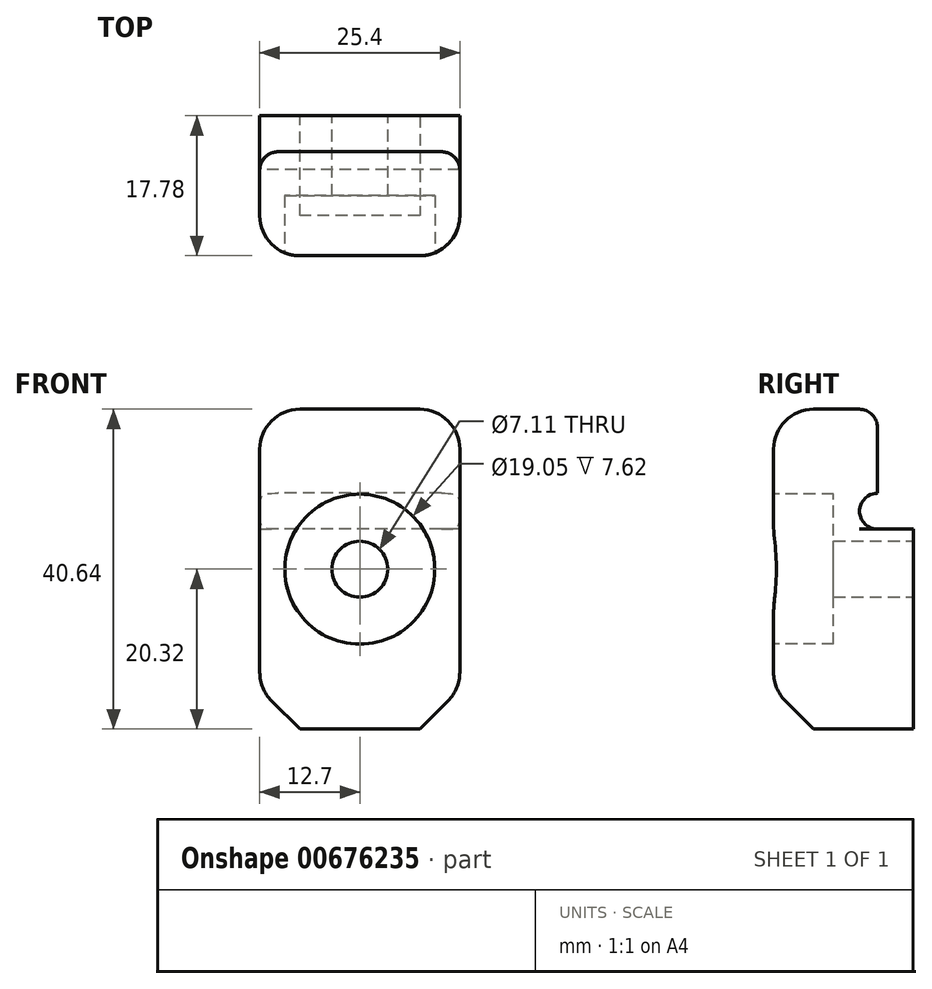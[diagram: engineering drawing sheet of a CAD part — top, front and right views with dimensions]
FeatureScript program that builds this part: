
annotation { "Feature Type Name" : "Feature", "Feature Type Description" : "" }
export const myFeature = defineFeature(function(context is Context, id is Id, definition is map)
    precondition{}
    {
        {
            var Q0;
            Q0=qCreatedBy(makeId("Right.planeOp"),FACE);
            var sketch = newSketch(context, id + "F0", { "sketchPlane" : qUnion([Q0])});
            skLineSegment(sketch, "E0.bottom", {"start": v(0, 0) * mm, "end": v(-4.57, 0) * mm});
            skLineSegment(sketch, "E0.top", {"start": v(0, -25.4) * mm, "end": v(-17.78, -25.4) * mm});
            skLineSegment(sketch, "E0.left", {"start": v(0, 0) * mm, "end": v(0, -25.4) * mm});
            skLineSegment(sketch, "E0.right", {"start": v(-17.78, 0) * mm, "end": v(-17.78, -25.4) * mm});
            skLineSegment(sketch, "E1.top", {"start": v(-17.78, 15.24) * mm, "end": v(-4.57, 15.24) * mm});
            skLineSegment(sketch, "E1.left", {"start": v(-17.78, 0) * mm, "end": v(-17.78, 15.24) * mm});
            skLineSegment(sketch, "E2", {"start": v(-9.82, 2.29) * mm, "end": v(19.83, 2.29) * mm, "construction": true});
            skArc(sketch, "E3", {"start": v(-4.57, 4.57) * mm, "mid": v(-6.86, 2.29) * mm, "end": v(-4.57, 0) * mm});
            skLineSegment(sketch, "E4.trimOffspring", {"start": v(-4.57, 4.57) * mm, "end": v(-4.57, 15.24) * mm});
            skSolve(sketch);
        }
        {
            var Q0;
            Q0=makeQuery(id+"F0.imprint","IMPRINT",FACE,{"disambiguationData":[TD([[makeQuery(id+"F0.imprint","IMPRINT",EDGE,{"derivedFrom":sQuery(id+"F0.wireOp",EDGE,"E0.bottom")}),1.0]])]});
            extrude(context, id + "F1", {"entities" : qUnion([Q0]), "depth" : 25.4 * mm, "offsetDistance" : 25.4 * mm});
        }
        {
            var Q0;
            Q0=makeQuery(id+"F1.opExtrude","SWEPT_FACE",FACE,{"disambiguationData":[OSD([sQuery(id+"F0.wireOp",EDGE,"E0.left")])]});
            var sketch = newSketch(context, id + "F2", { "sketchPlane" : qUnion([Q0])});
            skLineSegment(sketch, "E5", {"start": v(-12.7, 0) * mm, "end": v(-12.7, -25.4) * mm, "construction": true});
            skCircle(sketch, "E6", {"center": v(-12.7, -5.08) * mm, "radius": 3.56 * mm});
            skSolve(sketch);
        }
        {
            var Q0;
            Q0 = qSketchRegion(id + "F2", true);
            extrude(context, id + "F3", {"entities" : qUnion([Q0]), "operationType" : NewBodyOperationType.REMOVE, "endBound" : BoundingType.UP_TO_NEXT, "oppositeDirection" : true, "depth" : 25.4 * mm, "offsetDistance" : 25.4 * mm});
        }
        {
            var Q0;
            Q0=makeQuery(id+"F1.opExtrude","SWEPT_FACE",FACE,{"disambiguationData":[OSD([sQuery(id+"F0.wireOp",EDGE,"E0.right"),sQuery(id+"F0.wireOp",EDGE,"E1.left")])]});
            var sketch = newSketch(context, id + "F4", { "sketchPlane" : qUnion([Q0])});
            skCircle(sketch, "E7", {"center": v(12.7, -5.08) * mm, "radius": 9.52 * mm});
            skSolve(sketch);
        }
        {
            var Q0;
            Q0=makeQuery(id+"F4.imprint","IMPRINT",FACE,{"disambiguationData":[TD([[makeQuery(id+"F4.imprint","IMPRINT",EDGE,{"derivedFrom":sQuery(id+"F4.wireOp",EDGE,"E7")}),1.0]])]});
            extrude(context, id + "F5", {"entities" : qUnion([Q0]), "operationType" : NewBodyOperationType.REMOVE, "oppositeDirection" : true, "depth" : 7.62 * mm, "offsetDistance" : 25.4 * mm});
        }
        {
            var Q0;
            Q0=makeQuery(id+"F1.opExtrude","CAP_EDGE",EDGE,{"disambiguationData":[OSD([sQuery(id+"F0.wireOp",EDGE,"E0.right"),sQuery(id+"F0.wireOp",EDGE,"E1.left")])],"isStart":true});
            var Q1;
            Q1=makeQuery(id+"F1.opExtrude","CAP_EDGE",EDGE,{"disambiguationData":[OSD([sQuery(id+"F0.wireOp",EDGE,"E0.right"),sQuery(id+"F0.wireOp",EDGE,"E1.left")])],"isStart":false});
            var Q2;
            Q2=makeQuery(id+"F1.opExtrude","CAP_EDGE",EDGE,{"disambiguationData":[OSD([sQuery(id+"F0.wireOp",EDGE,"E1.top")])],"isStart":false});
            var Q3;
            Q3=makeQuery(id+"F1.opExtrude","SWEPT_EDGE",EDGE,{"disambiguationData":[OSD([sQuery(id+"F0.wireOp",EDGE,"E1.top"),sQuery(id+"F0.wireOp",EDGE,"E1.left")])]});
            var Q4;
            Q4=makeQuery(id+"F1.opExtrude","CAP_EDGE",EDGE,{"disambiguationData":[OSD([sQuery(id+"F0.wireOp",EDGE,"E1.top")])],"isStart":true});
            fillet(context, id + "F6", {"entities" : qUnion([Q0, Q1, Q2, Q3, Q4]), "radius" : 5.08 * mm, "tangentPropagation" : true, "allowEdgeOverflow" : false});
        }
        {
            var Q0;
            Q0=makeQuery(id+"F1.opExtrude","SWEPT_EDGE",EDGE,{"disambiguationData":[OSD([sQuery(id+"F0.wireOp",EDGE,"E0.top"),sQuery(id+"F0.wireOp",EDGE,"E0.right")])]});
            chamfer(context, id + "F7", {"entities" : qUnion([Q0]), "width" : 5.08 * mm, "tangentPropagation" : true});
        }
        {
            var Q0;
            {var subQ0=sQuery(id+"F0.wireOp",EDGE,"E0.right");Q0=makeQuery(id+"F7.opChamfer","BLEND_EDGE",EDGE,{"blendedFrom":[makeQuery(id+"F1.opExtrude","SWEPT_EDGE",EDGE,{"disambiguationData":[OSD([sQuery(id+"F0.wireOp",EDGE,"E0.top"),subQ0])]}),makeQuery(id+"F1.opExtrude","SWEPT_FACE",FACE,{"disambiguationData":[OSD([subQ0,sQuery(id+"F0.wireOp",EDGE,"E1.left")])]})],"blendedInto":[makeQuery(id+"F1.opExtrude","SWEPT_FACE",FACE,{"disambiguationData":[OSD([subQ0,sQuery(id+"F0.wireOp",EDGE,"E1.left")])]})]});}
            fillet(context, id + "F8", {"entities" : qUnion([Q0]), "radius" : 5.08 * mm, "tangentPropagation" : true, "allowEdgeOverflow" : false});
        }
        {
            var Q0;
            Q0=makeQuery(id+"F1.opExtrude","SWEPT_EDGE",EDGE,{"disambiguationData":[OSD([sQuery(id+"F0.wireOp",EDGE,"E1.top"),sQuery(id+"F0.wireOp",EDGE,"E4.trimOffspring")])]});
            fillet(context, id + "F9", {"entities" : qUnion([Q0]), "radius" : 2.33 * mm, "tangentPropagation" : true, "allowEdgeOverflow" : false});
        }
    });
